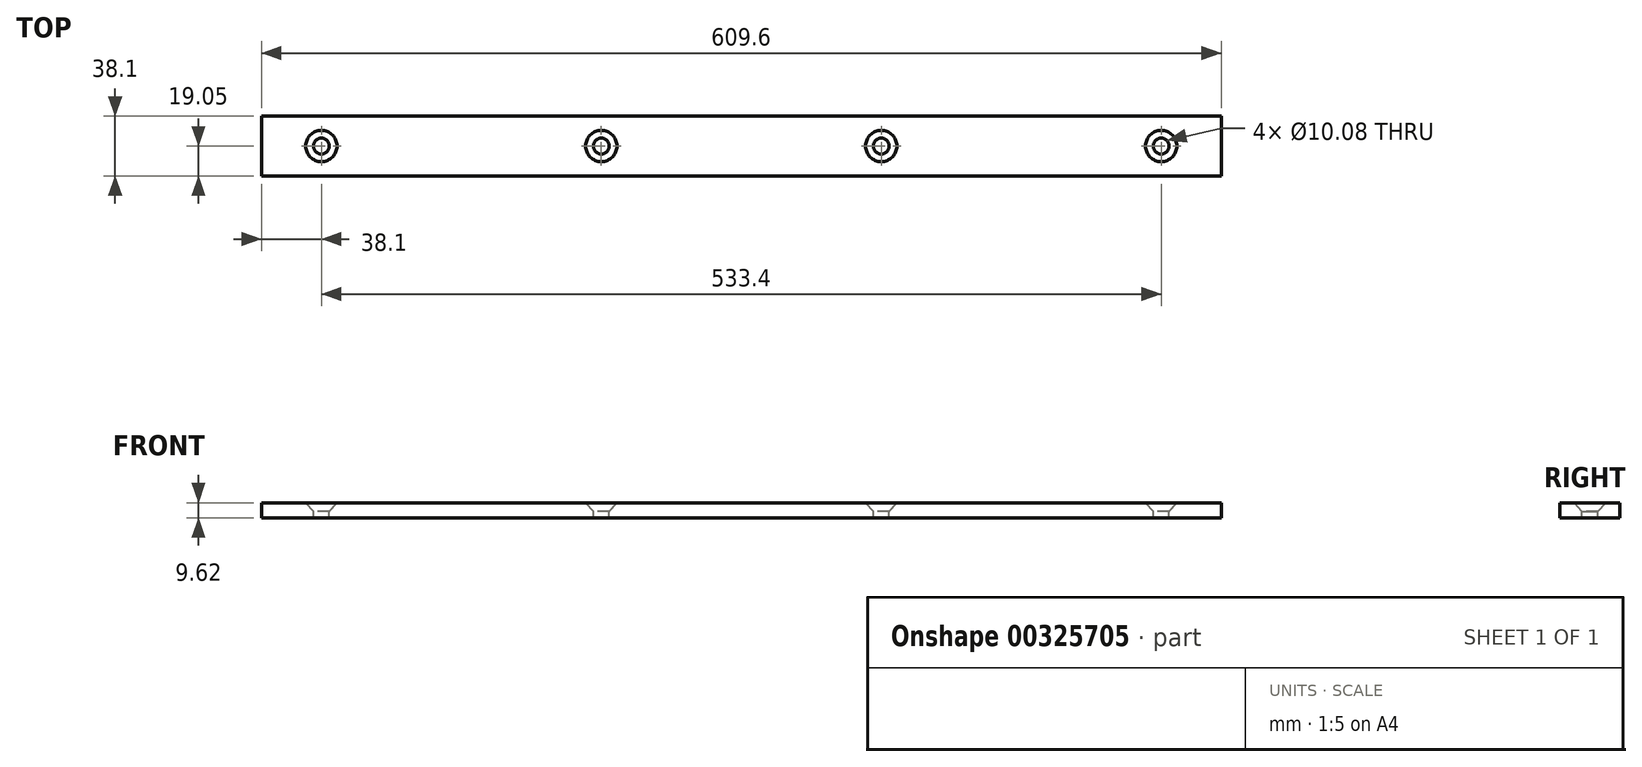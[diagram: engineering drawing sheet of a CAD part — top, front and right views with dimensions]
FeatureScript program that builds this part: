
annotation { "Feature Type Name" : "Feature", "Feature Type Description" : "" }
export const myFeature = defineFeature(function(context is Context, id is Id, definition is map)
    precondition{}
    {
        {
            var Q0;
            Q0=qCreatedBy(makeId("Top.planeOp"),FACE);
            var sketch = newSketch(context, id + "F0", { "sketchPlane" : qUnion([Q0])});
            skLineSegment(sketch, "E0.bottom", {"start": v(-304.8, 19.05) * mm, "end": v(304.8, 19.05) * mm});
            skLineSegment(sketch, "E0.top", {"start": v(-304.8, -19.05) * mm, "end": v(304.8, -19.05) * mm});
            skLineSegment(sketch, "E0.left", {"start": v(-304.8, 19.05) * mm, "end": v(-304.8, -19.05) * mm});
            skLineSegment(sketch, "E0.right", {"start": v(304.8, 19.05) * mm, "end": v(304.8, -19.05) * mm});
            skPoint(sketch, "E0.middle", {"position": v(0, 0) * mm});
            skSolve(sketch);
        }
        {
            var Q0;
            Q0=qSketchRegion(id+"F0",true);
            extrude(context, id + "F1", {"entities" : qUnion([Q0]), "endBound" : BoundingType.SYMMETRIC, "depth" : 9.63 * mm});
        }
        {
            var Q0;
            Q0=makeQuery(id+"F1.opExtrude","CAP_FACE",FACE,{"disambiguationData":[OSD([sQuery(id+"F0.wireOp",EDGE,"E0.bottom"),sQuery(id+"F0.wireOp",EDGE,"E0.top"),sQuery(id+"F0.wireOp",EDGE,"E0.left"),sQuery(id+"F0.wireOp",EDGE,"E0.right")])],"isStart":false});
            var sketch = newSketch(context, id + "F2", { "sketchPlane" : qUnion([Q0])});
            skLineSegment(sketch, "E1.0", {"start": v(-266.7, 19.05) * mm, "end": v(-266.7, -19.05) * mm, "construction": true});
            skLineSegment(sketch, "E2.0", {"start": v(-88.9, 19.05) * mm, "end": v(-88.9, -19.05) * mm, "construction": true});
            skLineSegment(sketch, "E3.0", {"start": v(88.9, 19.05) * mm, "end": v(88.9, -19.05) * mm, "construction": true});
            skLineSegment(sketch, "E4.0", {"start": v(266.7, 19.05) * mm, "end": v(266.7, -19.05) * mm, "construction": true});
            skLineSegment(sketch, "E5", {"start": v(-266.7, 0) * mm, "end": v(266.7, 0) * mm, "construction": true});
            skPoint(sketch, "E6", {"position": v(-266.7, 0) * mm});
            skPoint(sketch, "E7", {"position": v(-88.9, 0) * mm});
            skPoint(sketch, "E8", {"position": v(88.9, 0) * mm});
            skPoint(sketch, "E9", {"position": v(266.7, 0) * mm});
            skSolve(sketch);
        }
        {
            var Q0;
            Q0=sQuery(id+"F2.wireOp",VERTEX,"E6");
            var Q1;
            Q1=sQuery(id+"F2.wireOp",VERTEX,"E7");
            var Q2;
            Q2=sQuery(id+"F2.wireOp",VERTEX,"E8");
            var Q3;
            Q3=sQuery(id+"F2.wireOp",VERTEX,"E9");
            var Q4;
            Q4=makeQuery(id+"F1.opExtrude","SWEPT_BODY",BODY,{"disambiguationData":[OSD([sQuery(id+"F0.wireOp",EDGE,"E0.bottom"),sQuery(id+"F0.wireOp",EDGE,"E0.top"),sQuery(id+"F0.wireOp",EDGE,"E0.left"),sQuery(id+"F0.wireOp",EDGE,"E0.right")])]});
            hole(context, id + "F3", {"style" : HoleStyle.C_SINK, "endStyle" : HoleEndStyle.THROUGH, "standardTappedOrClearance" : lookupTablePath({ "standard" : "ANSI", "fit" : "Normal (ASME)", "size" : "3/8", "type" : "Clearance" }), "standardBlindInLast" : lookupTablePath({ "fit" : "Free", "standard" : "ANSI", "size" : "3/8", "type" : "Clearance" }), "holeDiameter" : 10.08 * mm, "cSinkDiameter" : 19.84 * mm, "cSinkAngle" : 82 * degree, "tappedDepth" : 14.29 * mm, "tapClearance" : 3, "locations" : qUnion([Q0, Q1, Q2, Q3]), "scope" : qUnion([Q4])});
        }
    });
